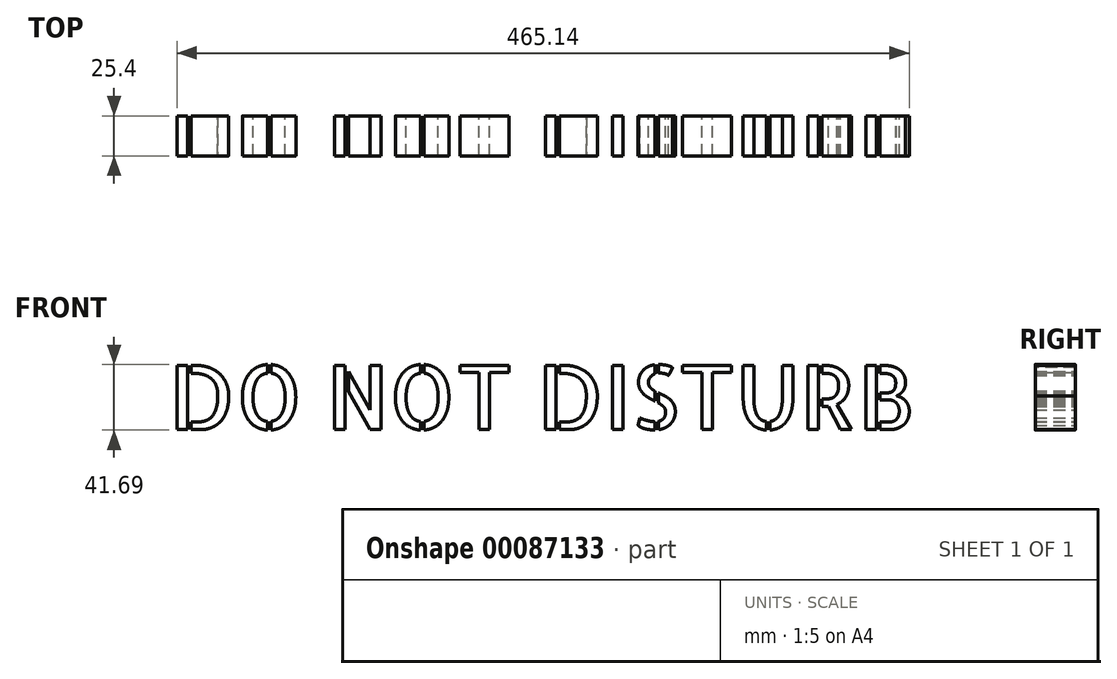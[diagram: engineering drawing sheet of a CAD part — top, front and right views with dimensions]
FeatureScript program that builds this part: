
annotation { "Feature Type Name" : "Feature", "Feature Type Description" : "" }
export const myFeature = defineFeature(function(context is Context, id is Id, definition is map)
    precondition{}
    {
        {
            var Q0;
            Q0=qCreatedBy(makeId("Front.planeOp"),FACE);
            var sketch = newSketch(context, id + "F0", { "sketchPlane" : qUnion([Q0])});
            skText(sketch, "E0", { "text": "DO NOT DISTURB", "fontName": "AllertaStencil-Regular.ttf"});
            const initialGuessF0  = {"E0": [-0.20673, -0.01012, 1, 0, 0.04077]};
            skSetInitialGuess(sketch, initialGuessF0);
            skSolve(sketch);
        }
        {
            var Q0;
            Q0 = qSketchRegion(id + "F0", true);
            extrude(context, id + "F1", {"entities" : qUnion([Q0]), "depth" : 25.4 * mm});
        }
    });
